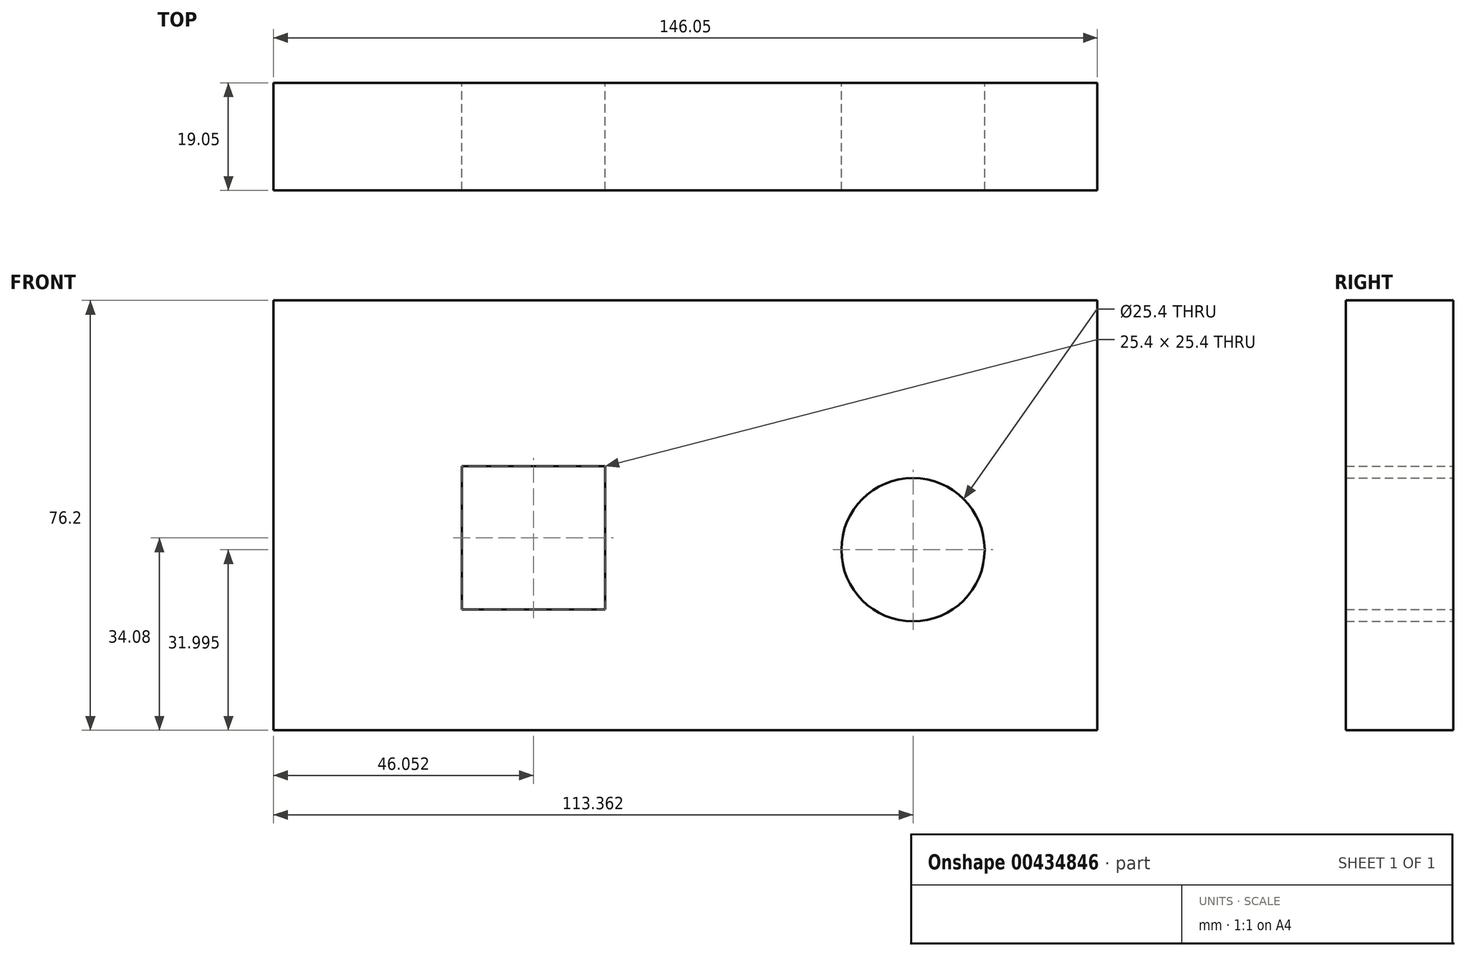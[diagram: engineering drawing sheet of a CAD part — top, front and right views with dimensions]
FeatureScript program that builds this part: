
annotation { "Feature Type Name" : "Feature", "Feature Type Description" : "" }
export const myFeature = defineFeature(function(context is Context, id is Id, definition is map)
    precondition{}
    {
        {
            var Q0;
            Q0=qCreatedBy(makeId("Front.planeOp"),FACE);
            var sketch = newSketch(context, id + "F0", { "sketchPlane" : qUnion([Q0])});
            skLineSegment(sketch, "E0.bottom", {"start": v(76.85, -76.2) * mm, "end": v(-69.2, -76.2) * mm});
            skLineSegment(sketch, "E0.top", {"start": v(76.85, 0) * mm, "end": v(-69.2, 0) * mm});
            skLineSegment(sketch, "E0.left", {"start": v(76.85, -76.2) * mm, "end": v(76.85, 0) * mm});
            skLineSegment(sketch, "E0.right", {"start": v(-69.2, -76.2) * mm, "end": v(-69.2, 0) * mm});
            skCircle(sketch, "E1", {"center": v(44.16, -44.2) * mm, "radius": 12.7 * mm});
            skLineSegment(sketch, "E2.bottom", {"start": v(-35.85, -54.82) * mm, "end": v(-10.45, -54.82) * mm});
            skLineSegment(sketch, "E2.top", {"start": v(-35.85, -29.42) * mm, "end": v(-10.45, -29.42) * mm});
            skLineSegment(sketch, "E2.left", {"start": v(-35.85, -54.82) * mm, "end": v(-35.85, -29.42) * mm});
            skLineSegment(sketch, "E2.right", {"start": v(-10.45, -54.82) * mm, "end": v(-10.45, -29.42) * mm});
            skSolve(sketch);
        }
        {
            var Q0;
            Q0=makeQuery(id+"F0.imprint","IMPRINT",FACE,{"disambiguationData":[TD([[makeQuery(id+"F0.imprint","IMPRINT",EDGE,{"derivedFrom":sQuery(id+"F0.wireOp",EDGE,"E0.bottom")}),-1.0]])]});
            extrude(context, id + "F1", {"entities" : qUnion([Q0]), "depth" : 19.05 * mm});
        }
    });
